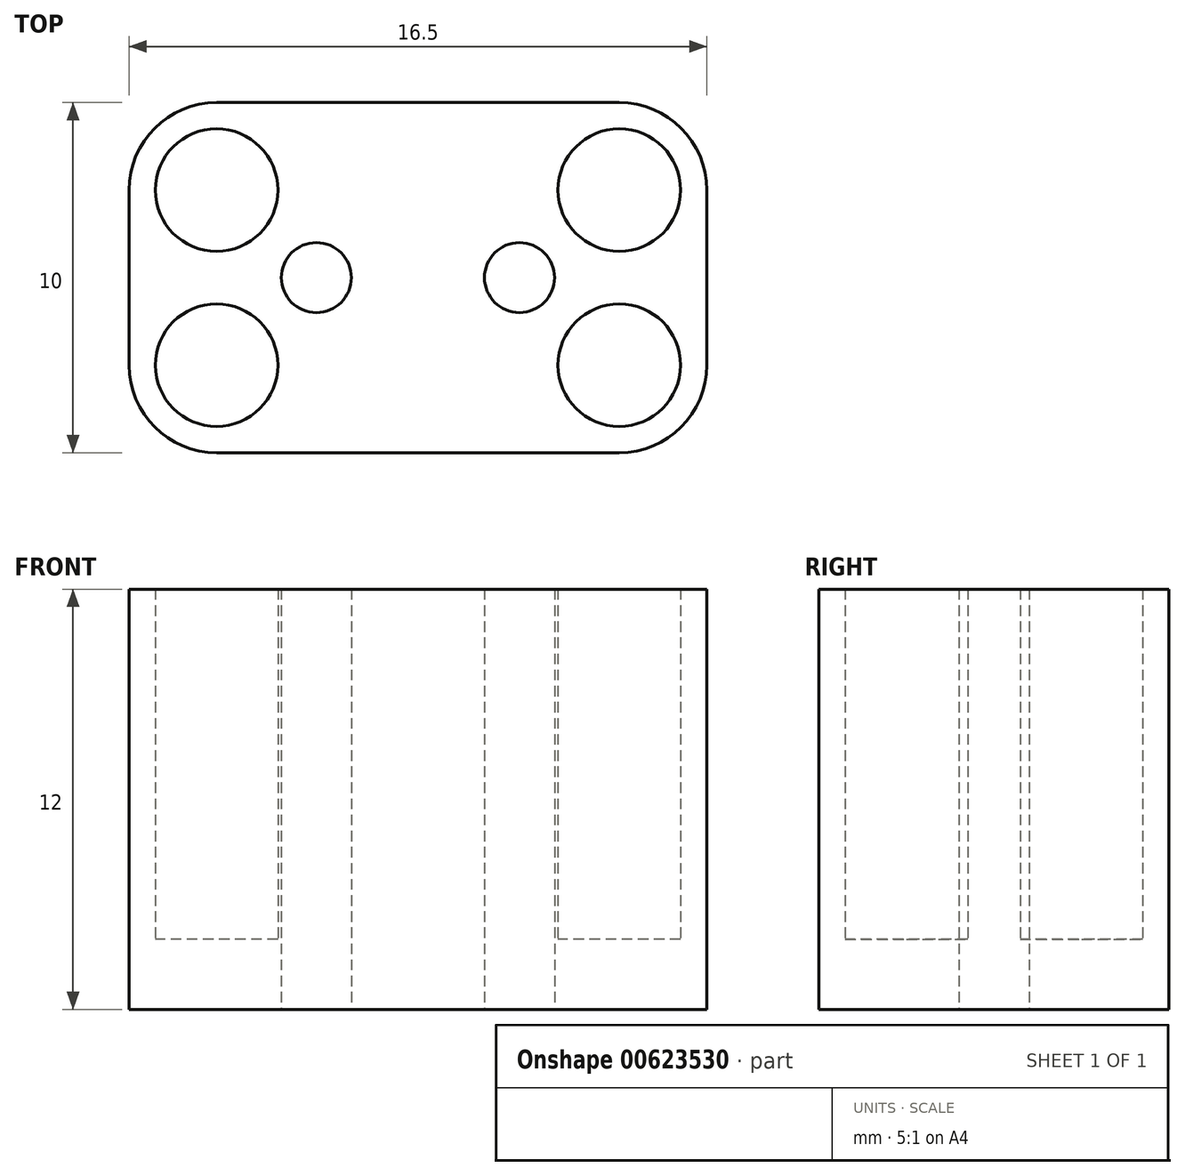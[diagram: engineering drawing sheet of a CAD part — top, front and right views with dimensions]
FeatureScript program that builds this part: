
annotation { "Feature Type Name" : "Feature", "Feature Type Description" : "" }
export const myFeature = defineFeature(function(context is Context, id is Id, definition is map)
    precondition{}
    {
        {
            var Q0;
            Q0=qCreatedBy(makeId("Top.planeOp"),FACE);
            var sketch = newSketch(context, id + "F0", { "sketchPlane" : qUnion([Q0])});
            skLineSegment(sketch, "E0.bottom", {"start": v(-5.75, 5) * mm, "end": v(5.75, 5) * mm});
            skLineSegment(sketch, "E0.top", {"start": v(-5.75, -5) * mm, "end": v(5.75, -5) * mm});
            skLineSegment(sketch, "E0.left", {"start": v(-8.25, 2.5) * mm, "end": v(-8.25, -2.5) * mm});
            skLineSegment(sketch, "E0.right", {"start": v(8.25, 2.5) * mm, "end": v(8.25, -2.5) * mm});
            skPoint(sketch, "E0.middle", {"position": v(0, 0) * mm});
            skLineSegment(sketch, "E1", {"start": v(-8.25, 0) * mm, "end": v(8.25, 0) * mm});
            skCircle(sketch, "E2", {"center": v(-2.9, 0) * mm, "radius": 1 * mm});
            skCircle(sketch, "E3", {"center": v(2.9, 0) * mm, "radius": 1 * mm});
            skPoint(sketch, "E4.visualSharp", {"position": v(-8.25, 5) * mm});
            skArc(sketch, "E4.filletArc", {"start": v(-5.75, 5) * mm, "mid": v(-7.52, 4.27) * mm, "end": v(-8.25, 2.5) * mm});
            skPoint(sketch, "E5.visualSharp", {"position": v(8.25, 5) * mm});
            skArc(sketch, "E5.filletArc", {"start": v(8.25, 2.5) * mm, "mid": v(7.52, 4.27) * mm, "end": v(5.75, 5) * mm});
            skPoint(sketch, "E6.visualSharp", {"position": v(8.25, -5) * mm});
            skArc(sketch, "E6.filletArc", {"start": v(5.75, -5) * mm, "mid": v(7.52, -4.27) * mm, "end": v(8.25, -2.5) * mm});
            skPoint(sketch, "E7.visualSharp", {"position": v(-8.25, -5) * mm});
            skArc(sketch, "E7.filletArc", {"start": v(-8.25, -2.5) * mm, "mid": v(-7.52, -4.27) * mm, "end": v(-5.75, -5) * mm});
            skCircle(sketch, "E8", {"center": v(-5.75, -2.5) * mm, "radius": 1.75 * mm});
            skCircle(sketch, "E9", {"center": v(5.75, -2.5) * mm, "radius": 1.75 * mm});
            skCircle(sketch, "E10", {"center": v(-5.75, 2.5) * mm, "radius": 1.75 * mm});
            skCircle(sketch, "E11", {"center": v(5.75, 2.5) * mm, "radius": 1.75 * mm});
            skSolve(sketch);
        }
        {
            var Q0;
            Q0=makeQuery(id+"F0.imprint","IMPRINT",FACE,{"disambiguationData":[TD([[makeQuery(id+"F0.imprint","IMPRINT",EDGE,{"derivedFrom":sQuery(id+"F0.wireOp",EDGE,"E0.top")}),1.0]])]});
            var Q1;
            Q1=makeQuery(id+"F0.imprint","IMPRINT",FACE,{"disambiguationData":[TD([[makeQuery(id+"F0.imprint","IMPRINT",EDGE,{"derivedFrom":sQuery(id+"F0.wireOp",EDGE,"E0.bottom")}),-1.0]])]});
            extrude(context, id + "F1", {"entities" : qUnion([Q0, Q1]), "depth" : 12 * mm, "offsetDistance" : 25 * mm});
        }
        {
            var Q0;
            Q0=makeQuery(id+"F0.imprint","IMPRINT",FACE,{"disambiguationData":[TD([[makeQuery(id+"F0.imprint","IMPRINT",EDGE,{"derivedFrom":sQuery(id+"F0.wireOp",EDGE,"E8")}),1.0]])]});
            var Q1;
            Q1=makeQuery(id+"F0.imprint","IMPRINT",FACE,{"disambiguationData":[TD([[makeQuery(id+"F0.imprint","IMPRINT",EDGE,{"derivedFrom":sQuery(id+"F0.wireOp",EDGE,"E9")}),1.0]])]});
            var Q2;
            Q2=makeQuery(id+"F0.imprint","IMPRINT",FACE,{"disambiguationData":[TD([[makeQuery(id+"F0.imprint","IMPRINT",EDGE,{"derivedFrom":sQuery(id+"F0.wireOp",EDGE,"E11")}),1.0]])]});
            var Q3;
            Q3=makeQuery(id+"F0.imprint","IMPRINT",FACE,{"disambiguationData":[TD([[makeQuery(id+"F0.imprint","IMPRINT",EDGE,{"derivedFrom":sQuery(id+"F0.wireOp",EDGE,"E10")}),1.0]])]});
            extrude(context, id + "F2", {"entities" : qUnion([Q0, Q1, Q2, Q3]), "operationType" : NewBodyOperationType.ADD, "depth" : 2 * mm, "offsetDistance" : 25 * mm});
        }
    });
